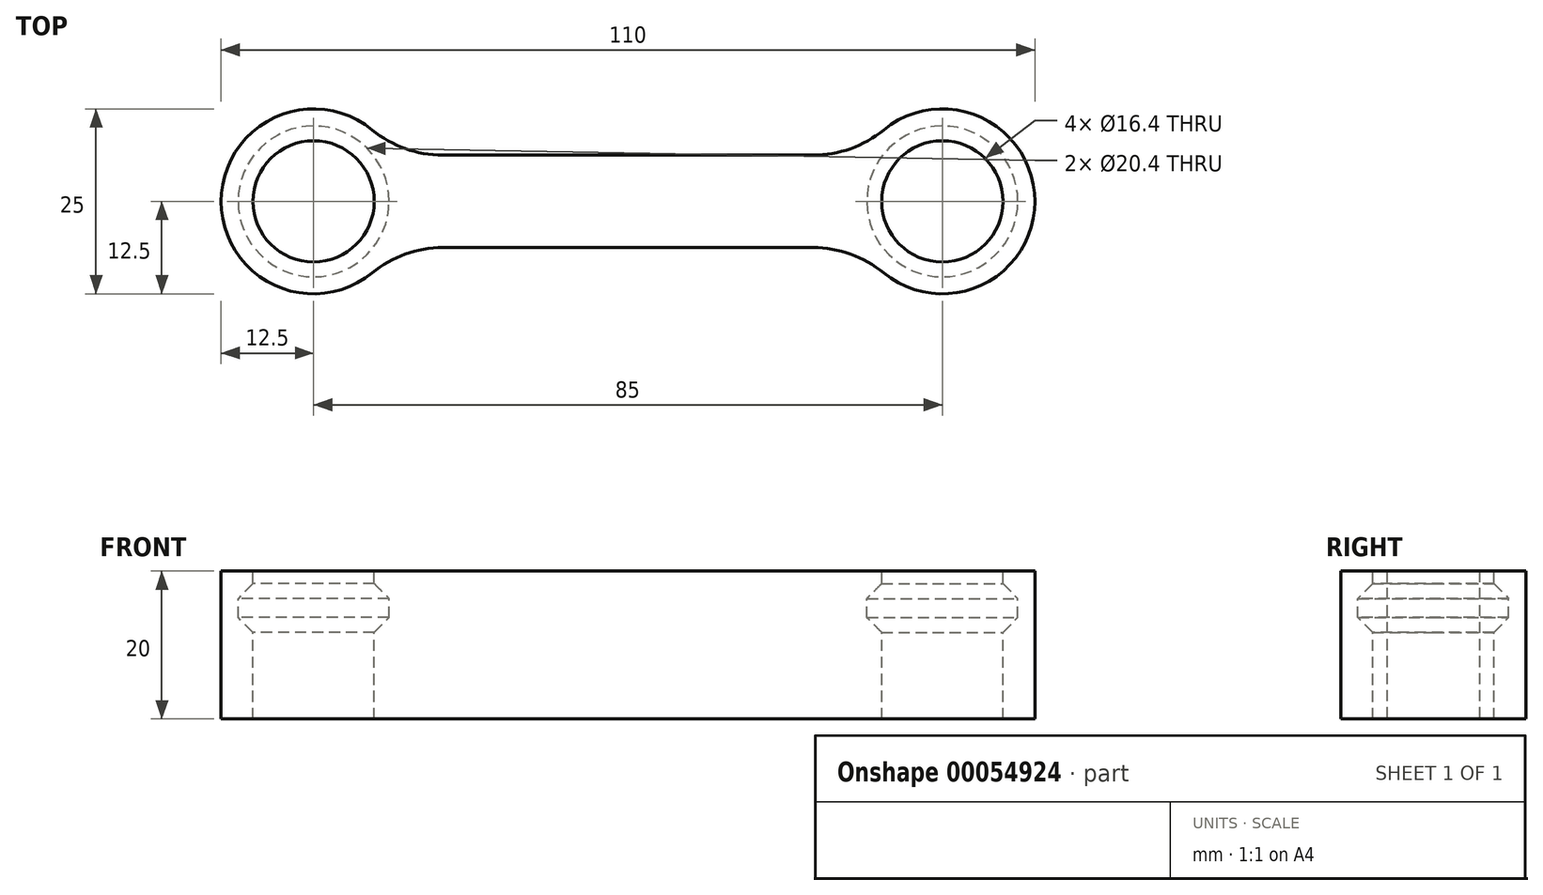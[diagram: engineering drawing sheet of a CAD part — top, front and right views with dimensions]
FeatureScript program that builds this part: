
annotation { "Feature Type Name" : "Feature", "Feature Type Description" : "" }
export const myFeature = defineFeature(function(context is Context, id is Id, definition is map)
    precondition{}
    {
        {
            var Q0;
            Q0=qCreatedBy(makeId("Front.planeOp"),FACE);
            var sketch = newSketch(context, id + "F0", { "sketchPlane" : qUnion([Q0])});
            skLineSegment(sketch, "E0.bottom", {"start": v(-35, 10) * mm, "end": v(-42.5, 10) * mm});
            skLineSegment(sketch, "E0.top", {"start": v(-35, 20) * mm, "end": v(-50, 20) * mm});
            skLineSegment(sketch, "E0.left", {"start": v(-35, 10) * mm, "end": v(-35, 20) * mm});
            skLineSegment(sketch, "E0.right", {"start": v(-50, 10) * mm, "end": v(-50, 20) * mm});
            skPoint(sketch, "E0.middle", {"position": v(-42.5, 15) * mm});
            skLineSegment(sketch, "E1", {"start": v(-50, 12) * mm, "end": v(-52, 14) * mm});
            skLineSegment(sketch, "E2", {"start": v(-52, 14) * mm, "end": v(-52, 16) * mm});
            skLineSegment(sketch, "E3", {"start": v(-52, 16) * mm, "end": v(-50, 18) * mm});
            skPoint(sketch, "E4", {"position": v(-52, 15) * mm});
            skLineSegment(sketch, "E5", {"start": v(-42.5, 20) * mm, "end": v(-42.5, 10) * mm, "construction": true});
            skLineSegment(sketch, "E6", {"start": v(-46, 20) * mm, "end": v(-46, 10) * mm});
            skLineSegment(sketch, "E7", {"start": v(-48, 2.45) * mm, "end": v(-46.58, 0) * mm});
            skLineSegment(sketch, "E8", {"start": v(-46.58, 0) * mm, "end": v(-50, 0) * mm});
            skLineSegment(sketch, "E9", {"start": v(-50, 0) * mm, "end": v(-50, 10) * mm});
            skLineSegment(sketch, "E10", {"start": v(-48, 2.45) * mm, "end": v(-48, 8) * mm});
            skLineSegment(sketch, "E11", {"start": v(-48, 8) * mm, "end": v(-46, 10) * mm});
            skLineSegment(sketch, "E12.0", {"start": v(-47.5, 7.8) * mm, "end": v(-46, 9.3) * mm});
            skLineSegment(sketch, "E12.1", {"start": v(-47.5, 2.58) * mm, "end": v(-47.5, 7.8) * mm});
            skLineSegment(sketch, "E12.2", {"start": v(-47.5, 2.58) * mm, "end": v(-46, 0) * mm});
            skLineSegment(sketch, "E13", {"start": v(-46, 10) * mm, "end": v(-46, 9.3) * mm});
            skLineSegment(sketch, "E14", {"start": v(-46, 9.3) * mm, "end": v(-46, 0) * mm});
            skLineSegment(sketch, "E15", {"start": v(0, 20) * mm, "end": v(0, 0) * mm, "construction": true});
            skLineSegment(sketch, "E16", {"start": v(-46, 0) * mm, "end": v(-45, 0) * mm});
            skLineSegment(sketch, "E17", {"start": v(-45, 0) * mm, "end": v(-45, 9.3) * mm});
            skLineSegment(sketch, "E18", {"start": v(-45, 11) * mm, "end": v(-45, 20) * mm});
            skLineSegment(sketch, "E19", {"start": v(-46, 10) * mm, "end": v(-45, 11) * mm});
            skLineSegment(sketch, "E20.trimOffspring", {"start": v(-46, 10) * mm, "end": v(-50, 10) * mm});
            skPoint(sketch, "E21.orphan", {"position": v(-45, 10) * mm});
            skLineSegment(sketch, "E22", {"start": v(-46, 9.3) * mm, "end": v(-45, 10.3) * mm});
            skLineSegment(sketch, "E23", {"start": v(-45, 10.3) * mm, "end": v(-45, 9.3) * mm});
            skSolve(sketch);
        }
        {
            var Q0;
            {var subQ0=sQuery(id+"F0.wireOp",EDGE,"E1");Q0=makeQuery(id+"F0.imprint","IMPRINT",FACE,{"disambiguationData":[TD([[makeQuery(id+"F0.imprint","IMPRINT",EDGE,{"derivedFrom":subQ0}),-1.0]])]});}
            var Q1;
            {var subQ7=sQuery(id+"F0.wireOp",EDGE,"E6");Q1=makeQuery(id+"F0.imprint","IMPRINT",FACE,{"disambiguationData":[TD([[makeQuery(id+"F0.imprint","IMPRINT",EDGE,{"derivedFrom":subQ7}),-1.0]])]});}
            var Q2;
            Q2=makeQuery(id+"F0.imprint","IMPRINT",FACE,{"disambiguationData":[TD([[makeQuery(id+"F0.imprint","IMPRINT",EDGE,{"derivedFrom":sQuery(id+"F0.wireOp",EDGE,"E7")}),-1.0]])]});
            var Q3;
            Q3=makeQuery(id+"F0.imprint","IMPRINT",FACE,{"disambiguationData":[TD([[makeQuery(id+"F0.imprint","IMPRINT",EDGE,{"derivedFrom":sQuery(id+"F0.wireOp",EDGE,"E12.0")}),-1.0]])]});
            var Q4;
            Q4=makeQuery(id+"F0.imprint","IMPRINT",FACE,{"disambiguationData":[TD([[makeQuery(id+"F0.imprint","IMPRINT",EDGE,{"derivedFrom":sQuery(id+"F0.wireOp",EDGE,"E14")}),1.0]])]});
            var Q5;
            {var subQ0=sQuery(id+"F0.wireOp",EDGE,"E6");Q5=makeQuery(id+"F0.imprint","IMPRINT",FACE,{"disambiguationData":[TD([[makeQuery(id+"F0.imprint","IMPRINT",EDGE,{"derivedFrom":subQ0}),1.0]])]});}
            var Q6;
            Q6=sQuery(id+"F0.wireOp",EDGE,"E5");
            revolve(context, id + "F1", {"entities" : qUnion([Q0, Q1, Q2, Q3, Q4, Q5]), "axis" : qUnion([Q6]), "revolveType" : RevolveType.FULL});
        }
        {
            var Q0;
            Q0=qCreatedBy(makeId("Front.planeOp"),FACE);
            var sketch = newSketch(context, id + "F2", { "sketchPlane" : qUnion([Q0])});
            skLineSegment(sketch, "E24.5", {"start": v(-50, 20) * mm, "end": v(-35, 20) * mm, "construction": true});
            skLineSegment(sketch, "E24.6", {"start": v(-52, 14) * mm, "end": v(-33, 14) * mm, "construction": true});
            skLineSegment(sketch, "E24.7", {"start": v(-50, 18) * mm, "end": v(-35, 18) * mm, "construction": true});
            skLineSegment(sketch, "E24.9.0", {"start": v(-35, 0) * mm, "end": v(-50, 0) * mm, "construction": true});
            skLineSegment(sketch, "E24.15", {"start": v(-46.58, 0) * mm, "end": v(-38.42, 0) * mm, "construction": true});
            skLineSegment(sketch, "E24.18", {"start": v(-45, 0) * mm, "end": v(-40, 0) * mm, "construction": true});
            skLineSegment(sketch, "E24.23.0", {"start": v(-39, 0) * mm, "end": v(-46, 0) * mm, "construction": true});
            skLineSegment(sketch, "E24.24", {"start": v(-50, 12) * mm, "end": v(-35, 12) * mm, "construction": true});
            skLineSegment(sketch, "E24.25", {"start": v(-52, 16) * mm, "end": v(-33, 16) * mm, "construction": true});
            skLineSegment(sketch, "E24.26", {"start": v(-45, 20) * mm, "end": v(-40, 20) * mm, "construction": true});
            skLineSegment(sketch, "E24.28.0", {"start": v(-50, 20) * mm, "end": v(-35, 20) * mm, "construction": true});
            skLineSegment(sketch, "E24.31", {"start": v(-50, 0) * mm, "end": v(-35, 0) * mm, "construction": true});
            skLineSegment(sketch, "E24.35", {"start": v(-46, 0) * mm, "end": v(-39, 0) * mm, "construction": true});
            skLineSegment(sketch, "E25", {"start": v(-50, 20) * mm, "end": v(-50, 18) * mm});
            skLineSegment(sketch, "E26", {"start": v(-50, 18) * mm, "end": v(-52, 16) * mm});
            skLineSegment(sketch, "E27", {"start": v(-52, 16) * mm, "end": v(-52, 14) * mm});
            skLineSegment(sketch, "E28", {"start": v(-52, 14) * mm, "end": v(-50, 12) * mm});
            skLineSegment(sketch, "E29", {"start": v(-50, 12) * mm, "end": v(-50, 0) * mm});
            skLineSegment(sketch, "E30", {"start": v(-50, 0) * mm, "end": v(-35, 0) * mm});
            skLineSegment(sketch, "E31", {"start": v(-35, 0) * mm, "end": v(-35, 12) * mm});
            skLineSegment(sketch, "E32", {"start": v(-35, 12) * mm, "end": v(-33, 14) * mm});
            skLineSegment(sketch, "E33", {"start": v(-33, 14) * mm, "end": v(-33, 16) * mm});
            skLineSegment(sketch, "E34", {"start": v(-33, 16) * mm, "end": v(-35, 18) * mm});
            skLineSegment(sketch, "E35", {"start": v(-35, 18) * mm, "end": v(-35, 20) * mm});
            skLineSegment(sketch, "E36", {"start": v(-35, 20) * mm, "end": v(-50, 20) * mm});
            skLineSegment(sketch, "E37.0", {"start": v(-50.7, 11.71) * mm, "end": v(-50.7, 0) * mm});
            skLineSegment(sketch, "E37.1", {"start": v(-32.3, 16.29) * mm, "end": v(-34.3, 18.29) * mm});
            skLineSegment(sketch, "E37.2", {"start": v(-32.3, 13.71) * mm, "end": v(-32.3, 16.29) * mm});
            skLineSegment(sketch, "E37.3", {"start": v(-34.3, 11.71) * mm, "end": v(-32.3, 13.71) * mm});
            skLineSegment(sketch, "E37.4", {"start": v(-34.3, 0) * mm, "end": v(-34.3, 11.71) * mm});
            skLineSegment(sketch, "E37.5", {"start": v(-34.3, 18.29) * mm, "end": v(-34.3, 20.7) * mm});
            skLineSegment(sketch, "E37.6", {"start": v(-50.7, 20.7) * mm, "end": v(-34.3, 20.7) * mm});
            skLineSegment(sketch, "E37.7", {"start": v(-50.7, 20.7) * mm, "end": v(-50.7, 18.29) * mm});
            skLineSegment(sketch, "E37.8", {"start": v(-50.7, 18.29) * mm, "end": v(-52.7, 16.29) * mm});
            skLineSegment(sketch, "E37.9", {"start": v(-52.7, 16.29) * mm, "end": v(-52.7, 13.71) * mm});
            skLineSegment(sketch, "E37.10", {"start": v(-52.7, 13.71) * mm, "end": v(-50.7, 11.71) * mm});
            skLineSegment(sketch, "E38", {"start": v(-50.7, 0) * mm, "end": v(-50, 0) * mm});
            skLineSegment(sketch, "E39", {"start": v(-35, 0) * mm, "end": v(-34.3, 0) * mm});
            skLineSegment(sketch, "E40", {"start": v(-42.5, 20.7) * mm, "end": v(-42.5, 0) * mm});
            skSolve(sketch);
        }
        {
            var Q0;
            Q0=qCreatedBy(makeId("Top.planeOp"),FACE);
            var sketch = newSketch(context, id + "F3", { "sketchPlane" : qUnion([Q0])});
            skCircle(sketch, "E41.0", {"center": v(-42.5, 0) * mm, "radius": 12.5 * mm});
            skLineSegment(sketch, "E42", {"start": v(-31.67, 6.25) * mm, "end": v(0, 6.25) * mm});
            skLineSegment(sketch, "E43", {"start": v(-31.67, -6.25) * mm, "end": v(0, -6.25) * mm});
            skLineSegment(sketch, "E44", {"start": v(0, 6.25) * mm, "end": v(0, -6.25) * mm});
            skArc(sketch, "E45", {"start": v(-34.57, 9.66) * mm, "mid": v(-30.1, 7.13) * mm, "end": v(-25.04, 6.25) * mm});
            skArc(sketch, "E46", {"start": v(-25.04, -6.25) * mm, "mid": v(-30.1, -7.13) * mm, "end": v(-34.57, -9.66) * mm});
            skSolve(sketch);
        }
        {
            var Q0;
            {var subQ0=sQuery(id+"F3.wireOp",EDGE,"E41.0");var subQ1=makeQuery(id+"F3.imprint","INTERSECT",VERTEX,{"derivedFrom":[subQ0,sQuery(id+"F3.wireOp",EDGE,"E42")]});Q0=makeQuery(id+"F3.imprint","IMPRINT",FACE,{"disambiguationData":[TD([[makeQuery(id+"F3.imprint","IMPRINT",EDGE,{"disambiguationData":[TD([[subQ1,-1.0]])],"derivedFrom":subQ0}),1.0]])]});}
            var Q1;
            {var subQ4=sQuery(id+"F3.wireOp",EDGE,"E44");Q1=makeQuery(id+"F3.imprint","IMPRINT",FACE,{"disambiguationData":[TD([[makeQuery(id+"F3.imprint","IMPRINT",EDGE,{"derivedFrom":subQ4}),-1.0]])]});}
            var Q2;
            {var subQ3=sQuery(id+"F3.wireOp",EDGE,"E45");Q2=makeQuery(id+"F3.imprint","IMPRINT",FACE,{"disambiguationData":[TD([[makeQuery(id+"F3.imprint","IMPRINT",EDGE,{"derivedFrom":subQ3}),-1.0]])]});}
            var Q3;
            {var subQ3=sQuery(id+"F3.wireOp",EDGE,"E46");Q3=makeQuery(id+"F3.imprint","IMPRINT",FACE,{"disambiguationData":[TD([[makeQuery(id+"F3.imprint","IMPRINT",EDGE,{"derivedFrom":subQ3}),-1.0]])]});}
            extrude(context, id + "F4", {"entities" : qUnion([Q0, Q1, Q2, Q3]), "depth" : 20 * mm});
        }
        {
            var Q0;
            {var subQ1=sQuery(id+"F2.wireOp",EDGE,"E25");Q0=makeQuery(id+"F2.imprint","IMPRINT",FACE,{"disambiguationData":[TD([[makeQuery(id+"F2.imprint","IMPRINT",EDGE,{"derivedFrom":subQ1}),-1.0]])]});}
            var Q1;
            {var subQ0=sQuery(id+"F2.wireOp",EDGE,"E25");Q1=makeQuery(id+"F2.imprint","IMPRINT",FACE,{"disambiguationData":[TD([[makeQuery(id+"F2.imprint","IMPRINT",EDGE,{"derivedFrom":subQ0}),1.0]])]});}
            var Q2;
            Q2=sQuery(id+"F2.wireOp",EDGE,"E40");
            revolve(context, id + "F5", {"operationType" : NewBodyOperationType.REMOVE, "entities" : qUnion([Q0, Q1]), "axis" : qUnion([Q2]), "revolveType" : RevolveType.FULL});
        }
        {
            var Q0;
            Q0=makeQuery(id+"F4.opExtrude","SWEPT_BODY",BODY,{"disambiguationData":[OSD([sQuery(id+"F3.wireOp",EDGE,"E41.0"),sQuery(id+"F3.wireOp",EDGE,"E42"),sQuery(id+"F3.wireOp",EDGE,"E43"),sQuery(id+"F3.wireOp",EDGE,"E44"),sQuery(id+"F3.wireOp",EDGE,"E45"),sQuery(id+"F3.wireOp",EDGE,"E46")])]});
            var Q1;
            Q1=makeQuery(id+"F1.opRevolve","SWEPT_BODY",BODY,{"disambiguationData":[OSD([sQuery(id+"F0.wireOp",EDGE,"E0.top"),sQuery(id+"F0.wireOp",EDGE,"E0.right"),sQuery(id+"F0.wireOp",EDGE,"E1"),sQuery(id+"F0.wireOp",EDGE,"E2"),sQuery(id+"F0.wireOp",EDGE,"E3"),sQuery(id+"F0.wireOp",EDGE,"E7"),sQuery(id+"F0.wireOp",EDGE,"E8"),sQuery(id+"F0.wireOp",EDGE,"E9"),sQuery(id+"F0.wireOp",EDGE,"E10"),sQuery(id+"F0.wireOp",EDGE,"E11"),sQuery(id+"F0.wireOp",EDGE,"E18"),sQuery(id+"F0.wireOp",EDGE,"E19")])]});
            var Q2;
            Q2=makeQuery(id+"F1.opRevolve","SWEPT_BODY",BODY,{"disambiguationData":[OSD([sQuery(id+"F0.wireOp",EDGE,"E12.0"),sQuery(id+"F0.wireOp",EDGE,"E12.1"),sQuery(id+"F0.wireOp",EDGE,"E12.2"),sQuery(id+"F0.wireOp",EDGE,"E16"),sQuery(id+"F0.wireOp",EDGE,"E17"),sQuery(id+"F0.wireOp",EDGE,"E22"),sQuery(id+"F0.wireOp",EDGE,"E23")])]});
            var Q3;
            Q3=makeQuery(id+"F4.opExtrude","SWEPT_FACE",FACE,{"disambiguationData":[OSD([sQuery(id+"F3.wireOp",EDGE,"E44")])]});
            mirror(context, id + "F6", {"operationType" : NewBodyOperationType.ADD, "entities" : qUnion([Q0, Q1, Q2]), "mirrorPlane" : qUnion([Q3])});
        }
    });
